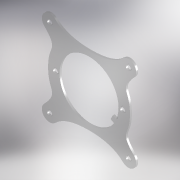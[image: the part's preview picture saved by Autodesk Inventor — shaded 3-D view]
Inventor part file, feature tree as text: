
AUTODESK INVENTOR PART (.ipt)
format: ipt  version: 2018 (Build 220112000, 112)  size: 230,912 bytes
history: native  units: mm
features: extrude x1, sketch x1
ambient origin geometry x8: Origin, YZ Plane, XZ Plane, XY Plane, X Axis, Y Axis, Z Axis, Center Point
bodies: Solid1 (feature_tree)
feature tree (2):
  extrude  "Extrusion1"  Depth=5.0mm
  sketch  "Sketch1"  dims[d0=60.0mm d4=5.0mm d5=68.282mm d6=80.0mm d7=80.0mm d8=5.0mm d9=5.0mm d10=5.0mm d11=5.0mm d12=8.0mm d13=45.0deg d14=5.0mm d15=5.0mm d16=5.0mm d17=18.0mm d18=3.0mm d19=0.0mm d20=5.0mm d21=26.0mm d22=4.782202mm]
